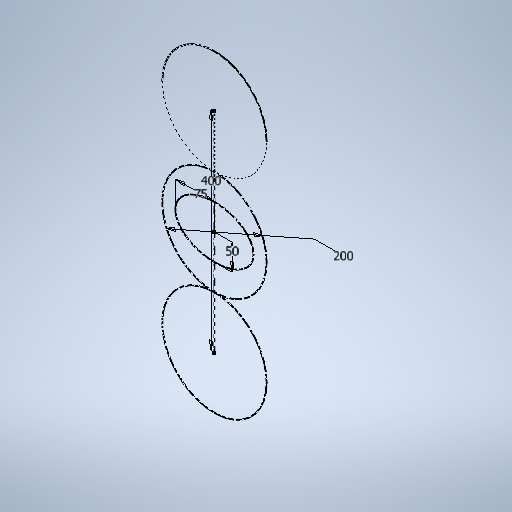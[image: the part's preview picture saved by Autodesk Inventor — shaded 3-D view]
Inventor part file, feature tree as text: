
AUTODESK INVENTOR PART (.ipt)
format: ipt  version: 2025.2 (Build 292293000, 293)  size: 256,000 bytes
history: native  units: in
note: dims shown in document units (in); Inventor stores cm internally (conversion verified against a paired STEP export)
features: sketch x1
ambient origin geometry x8: Origin, YZ Plane, XZ Plane, XY Plane, X Axis, Y Axis, Z Axis, Center Point
feature tree (1):
  sketch  "Sketch1"  dims[d0=15.748in d1=7.874in d2=1.9685in d3=2.9528in]
